# Revit family: PA7R
name_source: partatom
category: Lighting Fixtures
units: mm (PartAtom-declared; Revit-internal decimal feet)

## family parameters
Cut with Voids When Loaded = No
Host = Face
Light Source = Yes
OmniClass Number = 23.80.70.14.21
OmniClass Title = Street and Roadway Lighting
Part Type = Normal
Room Calculation Point = No
Round Connector Dimension = Use Diameter
Shared = No

## types (1)
- PA7R
    Apparent Load = 22 VA
    Color Filter = 16777215
    Default Elevation = 48 "
    Description = The Pavilion Impact Bollards are designed to protect pedestrians and property from the impact of errant or passing vehicles and are ASTM F3016 S20 rated (American Society for Testing and Materials). This is an architectural solution providing safety and security without the look of high security aesthetic.Pavilion redefines the bollard category with state of the art design, performance, and technology. An integral NEMA 3R enclosure, 2-Gang recessed box, and Bluetooth RGBW accent are just a few of the industry first features of Pavilion.
    Dimming Lamp Color Temperature Shift = <None>
    Emit Shape Visible in Rendering = No
    Emit from Circle Diameter = 5 "
    Features = ASTM F3016 S20 Impact Rated
• Elegant form factor blended with Performance Optics
• 44 inch OAH S20 Impact Rated Illuminated and Non-Illuminated Bollards
• IDA Dark Sky Compliant, No Up-light configuration
• Bluetooth enabled RGBW accent
    Fixture Finish = Color : Black
    Grill = No
    Lamp = LED
    Lens = No
    Lens Material = Glass
    Load Classification = Lighting
    Louver = No
    Manufacturer = KIM Lighting
    Model = Pavilion Impact Bollards
    NU = Yes
    Photometric Note = More IES files download in the Photometric Web link
    Photometric Web File = PA7R-CH1-12L-010-3K7.ies
    Power Factor = 1
    Tilt Angle = 90.00°
    URL = https://www.currentlighting.com
    Voltage = 120 V
    Watt = 22 W

## geometry (parser evidence)
native form markers: Blend x10, Sweep x6
no freeform markers — native parametric forms only
